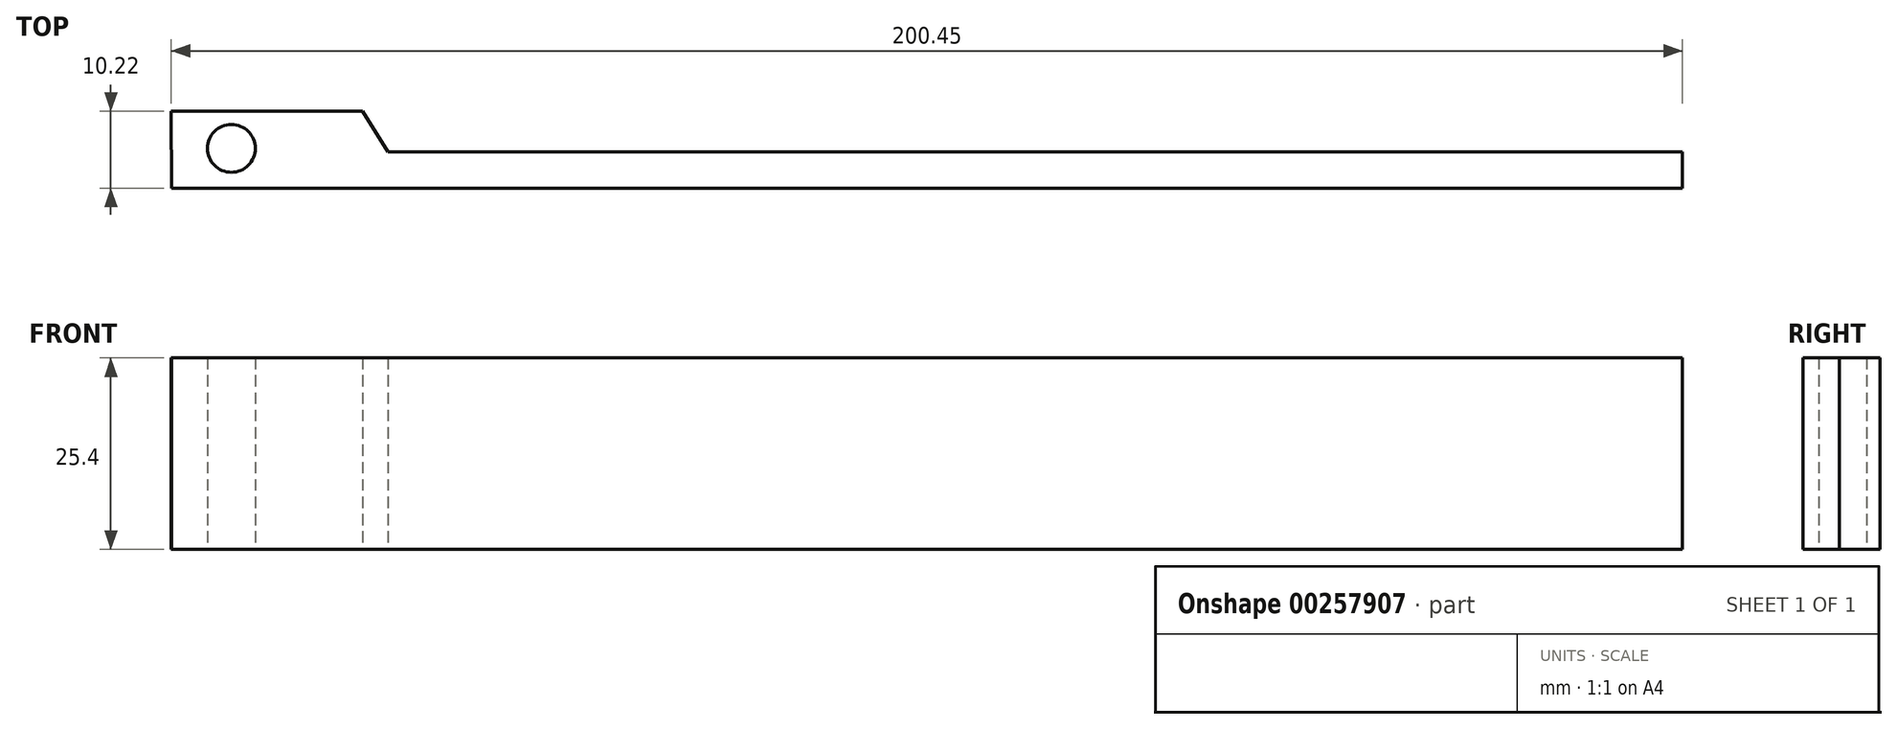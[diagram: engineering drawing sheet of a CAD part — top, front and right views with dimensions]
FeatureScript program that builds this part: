
annotation { "Feature Type Name" : "Feature", "Feature Type Description" : "" }
export const myFeature = defineFeature(function(context is Context, id is Id, definition is map)
    precondition{}
    {
        {
            var Q0;
            Q0=qCreatedBy(makeId("Top.planeOp"),FACE);
            var sketch = newSketch(context, id + "F0", { "sketchPlane" : qUnion([Q0])});
            skLineSegment(sketch, "E0", {"start": v(-124.04, -21.67) * mm, "end": v(76.36, -21.67) * mm});
            skLineSegment(sketch, "E1", {"start": v(-124.1, -11.45) * mm, "end": v(-98.7, -11.45) * mm});
            skPoint(sketch, "E2.end.orphan", {"position": v(-79.24, -11.45) * mm});
            skLineSegment(sketch, "E3", {"start": v(-98.7, -11.45) * mm, "end": v(-95.34, -16.85) * mm});
            skLineSegment(sketch, "E4", {"start": v(-95.34, -16.85) * mm, "end": v(-86.67, -11.45) * mm});
            skPoint(sketch, "E4.endSnap0", {"position": v(-111.4, -11.45) * mm});
            skLineSegment(sketch, "E5", {"start": v(-86.67, -11.45) * mm, "end": v(-79.24, -16.85) * mm});
            skLineSegment(sketch, "E6", {"start": v(-79.24, -16.85) * mm, "end": v(-75.32, -11.45) * mm});
            skLineSegment(sketch, "E7", {"start": v(-75.32, -11.45) * mm, "end": v(-67.9, -16.85) * mm});
            skLineSegment(sketch, "E8", {"start": v(-67.9, -16.85) * mm, "end": v(-63.98, -11.45) * mm});
            skLineSegment(sketch, "E9", {"start": v(-63.98, -11.45) * mm, "end": v(-56.56, -16.85) * mm});
            skLineSegment(sketch, "E10", {"start": v(-56.56, -16.85) * mm, "end": v(-52.64, -11.45) * mm});
            skLineSegment(sketch, "E11", {"start": v(-52.64, -11.45) * mm, "end": v(-45.21, -16.85) * mm});
            skLineSegment(sketch, "E12", {"start": v(-45.21, -16.85) * mm, "end": v(-41.3, -11.45) * mm});
            skLineSegment(sketch, "E13", {"start": v(-41.3, -11.45) * mm, "end": v(-33.87, -16.85) * mm});
            skLineSegment(sketch, "E14", {"start": v(-33.87, -16.85) * mm, "end": v(-29.96, -11.45) * mm});
            skLineSegment(sketch, "E15", {"start": v(-29.96, -11.45) * mm, "end": v(-22.53, -16.85) * mm});
            skLineSegment(sketch, "E16", {"start": v(-22.53, -16.85) * mm, "end": v(-18.61, -11.45) * mm});
            skLineSegment(sketch, "E17", {"start": v(-18.61, -11.45) * mm, "end": v(-11.19, -16.85) * mm});
            skLineSegment(sketch, "E18", {"start": v(-11.19, -16.85) * mm, "end": v(-7.27, -11.45) * mm});
            skLineSegment(sketch, "E19", {"start": v(-7.27, -11.45) * mm, "end": v(0.15, -16.85) * mm});
            skLineSegment(sketch, "E20", {"start": v(0.15, -16.85) * mm, "end": v(4.07, -11.45) * mm});
            skLineSegment(sketch, "E21", {"start": v(4.07, -11.45) * mm, "end": v(11.5, -16.85) * mm});
            skLineSegment(sketch, "E22", {"start": v(15.41, -11.45) * mm, "end": v(22.84, -16.85) * mm});
            skLineSegment(sketch, "E23", {"start": v(22.84, -16.85) * mm, "end": v(26.76, -11.45) * mm});
            skLineSegment(sketch, "E24", {"start": v(26.76, -11.45) * mm, "end": v(34.18, -16.85) * mm});
            skLineSegment(sketch, "E25", {"start": v(34.18, -16.85) * mm, "end": v(38.1, -11.45) * mm});
            skLineSegment(sketch, "E26", {"start": v(38.1, -11.45) * mm, "end": v(45.52, -16.85) * mm});
            skLineSegment(sketch, "E27", {"start": v(-124.04, -21.67) * mm, "end": v(-124.1, -11.45) * mm});
            skLineSegment(sketch, "E28", {"start": v(76.36, -21.67) * mm, "end": v(76.36, -11.45) * mm});
            skLineSegment(sketch, "E29", {"start": v(45.52, -16.85) * mm, "end": v(49.24, -11.73) * mm});
            skLineSegment(sketch, "E30", {"start": v(49.24, -11.73) * mm, "end": v(76.36, -11.45) * mm});
            skLineSegment(sketch, "E31", {"start": v(-124.04, -16.85) * mm, "end": v(76.36, -16.85) * mm});
            skSolve(sketch);
        }
        {
            var Q0;
            {var subQ6=sQuery(id+"F0.wireOp",EDGE,"E0");Q0=makeQuery(id+"F0.imprint","IMPRINT",FACE,{"disambiguationData":[TD([[makeQuery(id+"F0.imprint","IMPRINT",EDGE,{"derivedFrom":subQ6}),1.0]])]});}
            var sketch = newSketch(context, id + "F1", { "sketchPlane" : qUnion([Q0])});
            skCircle(sketch, "E32", {"center": v(-116.12, -16.39) * mm, "radius": 3.18 * mm});
            skCircle(sketch, "E33", {"center": v(67.78, -16.39) * mm, "radius": 3.18 * mm});
            skSolve(sketch);
        }
        {
            var Q0;
            {var subQ6=sQuery(id+"F0.wireOp",EDGE,"E0");Q0=makeQuery(id+"F0.imprint","IMPRINT",FACE,{"disambiguationData":[TD([[makeQuery(id+"F0.imprint","IMPRINT",EDGE,{"derivedFrom":subQ6}),1.0]])]});}
            var Q1;
            Q1=makeQuery(id+"F1.imprint","IMPRINT",FACE,{"disambiguationData":[TD([[makeQuery(id+"F1.imprint","IMPRINT",EDGE,{"derivedFrom":sQuery(id+"F1.wireOp",EDGE,"E32")}),1.0]])]});
            var Q2;
            Q2=makeQuery(id+"F1.imprint","IMPRINT",FACE,{"disambiguationData":[TD([[makeQuery(id+"F1.imprint","IMPRINT",EDGE,{"derivedFrom":sQuery(id+"F1.wireOp",EDGE,"E32")}),1.0]])]});
            var Q3;
            Q3=makeQuery(id+"F1.imprint","IMPRINT",FACE,{"disambiguationData":[TD([[makeQuery(id+"F1.imprint","IMPRINT",EDGE,{"derivedFrom":sQuery(id+"F1.wireOp",EDGE,"E32")}),1.0]])]});
            extrude(context, id + "F2", {"entities" : qUnion([Q0, Q1, Q2, Q3]), "depth" : 25.4 * mm});
        }
    });
